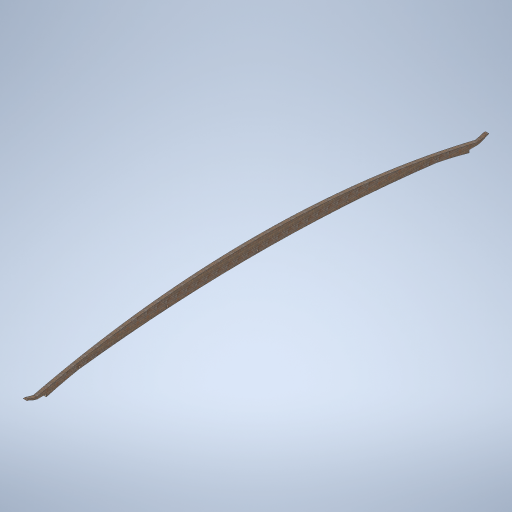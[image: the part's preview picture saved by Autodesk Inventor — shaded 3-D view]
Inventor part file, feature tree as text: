
AUTODESK INVENTOR PART (.ipt)
format: ipt  version: 2024.2 (Build 282272000, 272)  size: 421,376 bytes
history: native  units: mm
features: sketch x11, extrude x7
ambient origin geometry x8: Origin, YZ Plane, XZ Plane, XY Plane, X Axis, Y Axis, Z Axis, Center Point
bodies: Solid1 (feature_tree)
feature tree (18):
  extrude  "Extrusion1"  Depth=20000.0mm
  sketch  "Sketch2"  dims[d2=20000.0mm d3=0.0mm]
  sketch  "Sketch4"  dims[d4=0.0mm d5=2500.0mm]
  sketch  "Sketch5"  dims[d6=900.0mm d7=120.0mm]
  extrude  "Extrusion2"  TaperAngle=0.0deg  [1 undecoded]
  extrude  "Extrusion3"  Depth=2500.0mm
  extrude  "Extrusion4"  Depth=120.0mm
  sketch  "Sketch10"  dims[d14=150.0mm d15=150.0mm d16=0.0mm d17=0.0mm]
  extrude  "Extrusion5"  TaperAngle=90.0deg  [1 undecoded]
  extrude  "Extrusion7"  Depth=200.0mm
  extrude  "Extrusion8"  Depth=120000.0mm
  sketch  "Sketch1"  dims[d0=200000.0mm d1=20000.0mm]
  sketch  "Sketch7"  dims[d8=210.0mm d9=90.0deg]
  sketch  "Sketch8"  dims[d10=4000.0mm d11=200.0mm]
  sketch  "Sketch9"  dims[d12=60.0mm d13=120000.0mm]
  sketch  "Sketch11"  dims[d20=300.0mm d21=0.0mm]
  sketch  "Sketch12"  dims[d22=300.0mm]
  sketch  "Sketch13"  dims[d23=17500.0mm d24=90.0deg d25=17500.0mm d26=180.0deg d27=130000.0mm d28=300.0mm d29=0.0mm d30=29.670597mm d31=1.745329mm d32=1000.0mm d33=0.0mm d34=7000.0mm d35=90.0deg d36=3000.0mm d37=3000.0mm d38=6000.0mm d39=8000.0mm d40=3000.0mm d41=6000.0mm d42=100.0mm d43=200.0mm d44=100.0mm d45=200.0mm d46=100.0mm d47=200.0mm d48=300.0mm d49=0.0mm d53=35000.0mm d54=300.0mm d55=0.0mm d56=85000.0mm d57=300.0mm d58=0.0mm]
note: 2 required parameter values undecoded (feature->parameter linkage not recoverable at this tier; creation-order binding heuristic only, values carry confidence <= 0.55)
